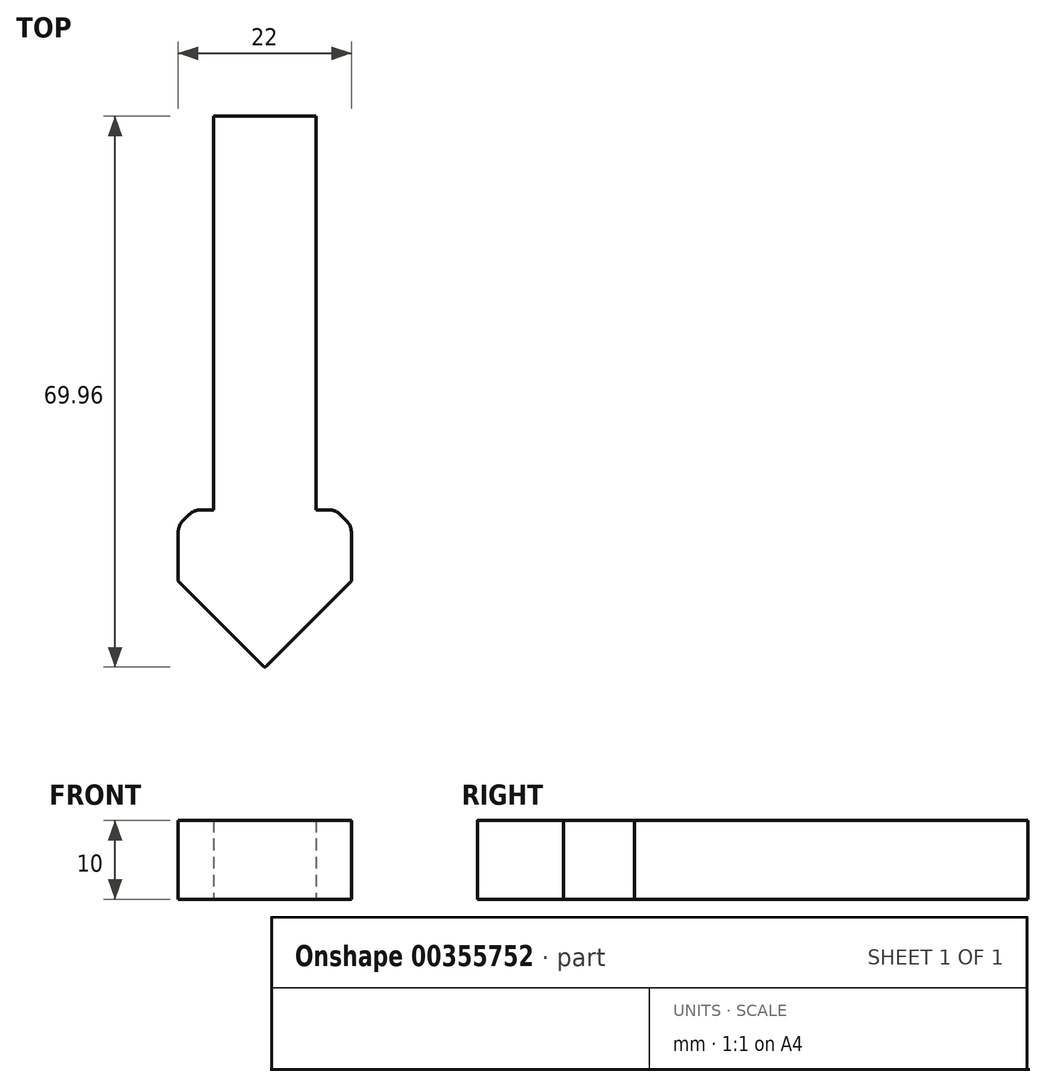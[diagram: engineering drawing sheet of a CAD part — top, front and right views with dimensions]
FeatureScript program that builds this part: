
annotation { "Feature Type Name" : "Feature", "Feature Type Description" : "" }
export const myFeature = defineFeature(function(context is Context, id is Id, definition is map)
    precondition{}
    {
        {
            var Q0;
            Q0=qCreatedBy(makeId("Top.planeOp"),FACE);
            var sketch = newSketch(context, id + "F0", { "sketchPlane" : qUnion([Q0])});
            skLineSegment(sketch, "E0", {"start": v(6.5, 70) * mm, "end": v(0, 70) * mm});
            skLineSegment(sketch, "E1", {"start": v(6.5, 20) * mm, "end": v(11, 20) * mm});
            skLineSegment(sketch, "E2", {"start": v(11, 20) * mm, "end": v(11, 11) * mm});
            skLineSegment(sketch, "E3", {"start": v(11, 11) * mm, "end": v(0, 0) * mm});
            skLineSegment(sketch, "E4", {"start": v(6.5, 20) * mm, "end": v(6.5, 70) * mm});
            skLineSegment(sketch, "E5.MirrorCS", {"start": v(-6.5, 20) * mm, "end": v(-11, 20) * mm});
            skLineSegment(sketch, "E6.MirrorCS", {"start": v(-6.5, 70) * mm, "end": v(0, 70) * mm});
            skLineSegment(sketch, "E7.MirrorCS", {"start": v(-11, 20) * mm, "end": v(-11, 11) * mm});
            skLineSegment(sketch, "E8.MirrorCS", {"start": v(-11, 11) * mm, "end": v(0, 0) * mm});
            skLineSegment(sketch, "E9.MirrorCS", {"start": v(-6.5, 20) * mm, "end": v(-6.5, 70) * mm});
            skSolve(sketch);
        }
        {
            var Q0;
            Q0=makeQuery(id+"F0.imprint","IMPRINT",FACE,{"disambiguationData":[TD([[makeQuery(id+"F0.imprint","IMPRINT",EDGE,{"derivedFrom":sQuery(id+"F0.wireOp",EDGE,"E0")}),1.0]])]});
            extrude(context, id + "F1", {"entities" : qUnion([Q0]), "depth" : 10 * mm});
        }
        {
            var Q0;
            Q0=makeQuery(id+"F1.opExtrude","SWEPT_EDGE",EDGE,{"disambiguationData":[OSD([sQuery(id+"F0.wireOp",EDGE,"E3"),sQuery(id+"F0.wireOp",EDGE,"E8.MirrorCS")])]});
            fillet(context, id + "F2", {"entities" : qUnion([Q0]), "radius" : 0.1 * mm, "tangentPropagation" : true, "allowEdgeOverflow" : false});
        }
        {
            var Q0;
            Q0=makeQuery(id+"F1.opExtrude","SWEPT_EDGE",EDGE,{"disambiguationData":[OSD([sQuery(id+"F0.wireOp",EDGE,"E5.MirrorCS"),sQuery(id+"F0.wireOp",EDGE,"E7.MirrorCS")])]});
            var Q1;
            Q1=makeQuery(id+"F1.opExtrude","SWEPT_EDGE",EDGE,{"disambiguationData":[OSD([sQuery(id+"F0.wireOp",EDGE,"E1"),sQuery(id+"F0.wireOp",EDGE,"E2")])]});
            chamfer(context, id + "F3", {"entities" : qUnion([Q0, Q1]), "width" : 2 * mm, "tangentPropagation" : true});
        }
        {
            var Q0;
            {var subQ0=sQuery(id+"F0.wireOp",EDGE,"E1");Q0=makeQuery(id+"F3.opChamfer","BLEND_EDGE",EDGE,{"blendedFrom":[makeQuery(id+"F1.opExtrude","SWEPT_EDGE",EDGE,{"disambiguationData":[OSD([subQ0,sQuery(id+"F0.wireOp",EDGE,"E2")])]}),makeQuery(id+"F1.opExtrude","SWEPT_FACE",FACE,{"disambiguationData":[OSD([subQ0])]})],"blendedInto":[makeQuery(id+"F1.opExtrude","SWEPT_FACE",FACE,{"disambiguationData":[OSD([subQ0])]})]});}
            var Q1;
            {var subQ0=sQuery(id+"F0.wireOp",EDGE,"E2");Q1=makeQuery(id+"F3.opChamfer","BLEND_EDGE",EDGE,{"blendedFrom":[makeQuery(id+"F1.opExtrude","SWEPT_EDGE",EDGE,{"disambiguationData":[OSD([sQuery(id+"F0.wireOp",EDGE,"E1"),subQ0])]}),makeQuery(id+"F1.opExtrude","SWEPT_FACE",FACE,{"disambiguationData":[OSD([subQ0])]})],"blendedInto":[makeQuery(id+"F1.opExtrude","SWEPT_FACE",FACE,{"disambiguationData":[OSD([subQ0])]})]});}
            var Q2;
            {var subQ0=sQuery(id+"F0.wireOp",EDGE,"E5.MirrorCS");Q2=makeQuery(id+"F3.opChamfer","BLEND_EDGE",EDGE,{"blendedFrom":[makeQuery(id+"F1.opExtrude","SWEPT_EDGE",EDGE,{"disambiguationData":[OSD([subQ0,sQuery(id+"F0.wireOp",EDGE,"E7.MirrorCS")])]}),makeQuery(id+"F1.opExtrude","SWEPT_FACE",FACE,{"disambiguationData":[OSD([subQ0])]})],"blendedInto":[makeQuery(id+"F1.opExtrude","SWEPT_FACE",FACE,{"disambiguationData":[OSD([subQ0])]})]});}
            var Q3;
            {var subQ0=sQuery(id+"F0.wireOp",EDGE,"E7.MirrorCS");Q3=makeQuery(id+"F3.opChamfer","BLEND_EDGE",EDGE,{"blendedFrom":[makeQuery(id+"F1.opExtrude","SWEPT_EDGE",EDGE,{"disambiguationData":[OSD([sQuery(id+"F0.wireOp",EDGE,"E5.MirrorCS"),subQ0])]}),makeQuery(id+"F1.opExtrude","SWEPT_FACE",FACE,{"disambiguationData":[OSD([subQ0])]})],"blendedInto":[makeQuery(id+"F1.opExtrude","SWEPT_FACE",FACE,{"disambiguationData":[OSD([subQ0])]})]});}
            fillet(context, id + "F4", {"entities" : qUnion([Q0, Q1, Q2, Q3]), "radius" : 2 * mm, "tangentPropagation" : true, "allowEdgeOverflow" : false});
        }
    });
